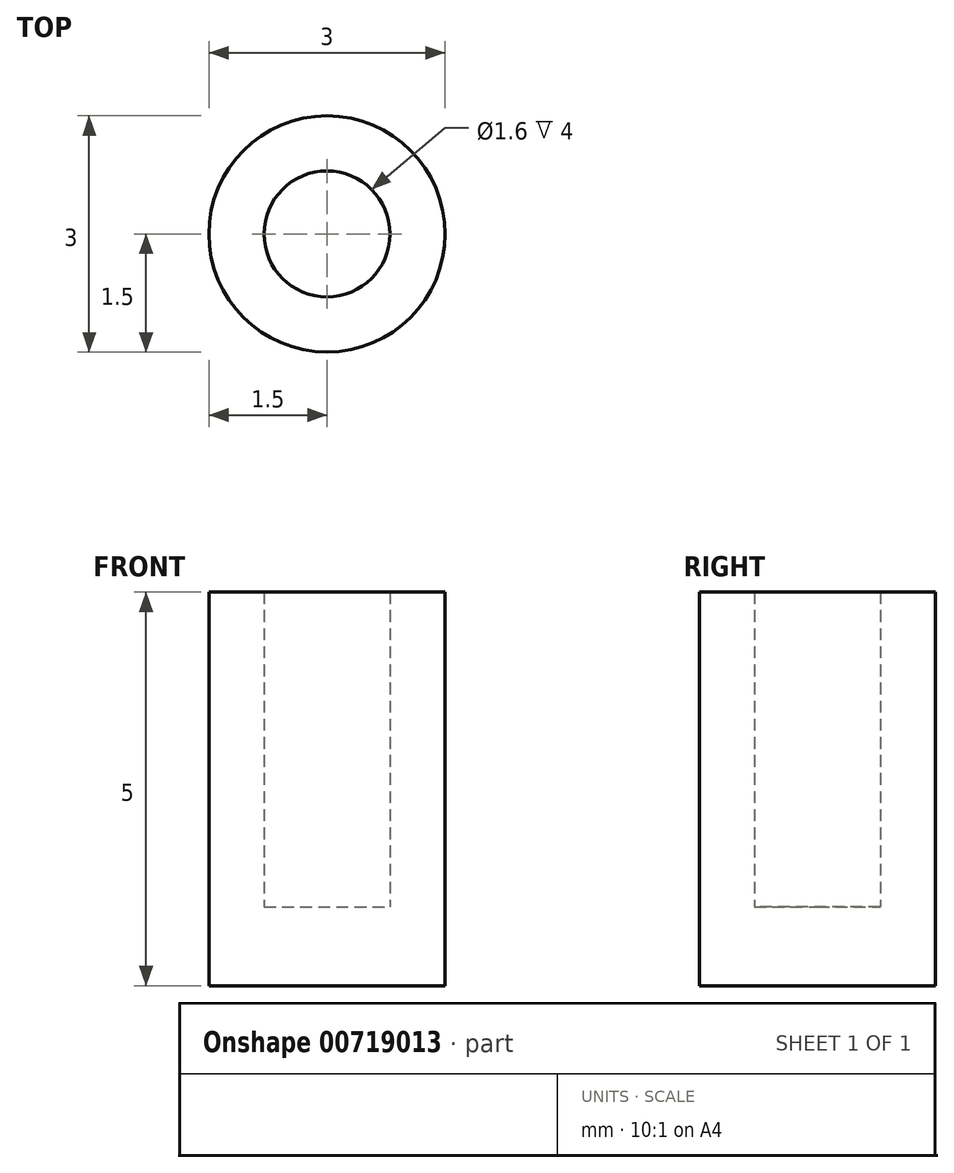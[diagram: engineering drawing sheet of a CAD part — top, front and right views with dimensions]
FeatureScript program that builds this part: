
annotation { "Feature Type Name" : "Feature", "Feature Type Description" : "" }
export const myFeature = defineFeature(function(context is Context, id is Id, definition is map)
    precondition{}
    {
        {
            var Q0;
            Q0=qCreatedBy(makeId("Front.planeOp"),FACE);
            var sketch = newSketch(context, id + "F0", { "sketchPlane" : qUnion([Q0])});
            skLineSegment(sketch, "E0", {"start": v(0, 0) * mm, "end": v(1.5, 0) * mm});
            skLineSegment(sketch, "E1", {"start": v(1.5, 0) * mm, "end": v(1.5, 5) * mm});
            skLineSegment(sketch, "E2", {"start": v(1.5, 5) * mm, "end": v(0.8, 5) * mm});
            skLineSegment(sketch, "E3", {"start": v(0.8, 5) * mm, "end": v(0.8, 1) * mm});
            skLineSegment(sketch, "E4", {"start": v(0, 0) * mm, "end": v(0, 1) * mm});
            skLineSegment(sketch, "E5", {"start": v(0.8, 1) * mm, "end": v(0, 1) * mm});
            skLineSegment(sketch, "E6", {"start": v(0, 0) * mm, "end": v(0, 6.36) * mm, "construction": true});
            skSolve(sketch);
        }
        {
            var Q0;
            Q0=makeQuery(id+"F0.imprint","IMPRINT",FACE,{"disambiguationData":[TD([[makeQuery(id+"F0.imprint","IMPRINT",EDGE,{"derivedFrom":sQuery(id+"F0.wireOp",EDGE,"E0")}),1.0]])]});
            var Q1;
            Q1=sQuery(id+"F0.wireOp",EDGE,"E6");
            revolve(context, id + "F1", {"surfaceOperationType" : NewSurfaceOperationType.NEW, "entities" : qUnion([Q0]), "axis" : qUnion([Q1]), "revolveType" : RevolveType.FULL});
        }
    });
